# Revit family: Солід_Eng
name_source: partatom
category: Mechanical Equipment
units: mm (PartAtom-declared; Revit-internal decimal feet)

## family parameters
Always vertical = Yes
Classification = None
Cut with Voids When Loaded = No
Part Type = Normal
Room Calculation Point = No
Round Connector Dimension = Use Diameter
Shared = No
Work Plane-Based = No

## types (4) — shared parameters
00_20_Manufacturer = Vents
00_20_Name = Axial fan
Amperage = 0 A
Casing Material = Plastic, opaque, white
L1 = 38 mm  [stored 0.124672 ft]
Load Classification = HVAC
Maintenance zone material = <By Category>
Manufacturer = Vents
Number of Fase = 1
URL = https://ventilation-system.com
Voltage = 230 V
zero-valued in all types: Default Elevation

## per-type parameters (varying)
| type | B | D | Diameter | Dy | Frequency | H | Height | L | L2 | Length | Maximum Air Flow | Power | Sound pressure level at 3 m distance | Weight | Width |
| 100 Solid | 160 mm  [stored 0.524934 ft] | 100 mm  [stored 0.328084 ft] | 100 mm  [stored 0.328084 ft] | 95 mm  [stored 0.31168 ft] | 50 Hz | 160 mm  [stored 0.524934 ft] | 160 mm  [stored 0.524934 ft] | 79 mm | 41 mm  [stored 0.134514 ft] | 79 mm | 85.0 m³/h | 8 W | 27 дБА | 0.51 kg | 160 mm  [stored 0.524934 ft] |
| 125 Solid | 180 mm  [stored 0.590551 ft] | 125 mm  [stored 0.410105 ft] | 125 mm  [stored 0.410105 ft] | 120 mm  [stored 0.393701 ft] | 50 Hz | 180 mm  [stored 0.590551 ft] | 180 mm  [stored 0.590551 ft] | 85 mm  [stored 0.278871 ft] | 47 mm  [stored 0.154199 ft] | 85 mm  [stored 0.278871 ft] | 155.0 m³/h | 18 W | 32 дБА | 0.75 kg | 180 mm  [stored 0.590551 ft] |
| 100 Solid (220 В/60 Hz) | 160 mm  [stored 0.524934 ft] | 100 mm  [stored 0.328084 ft] | 100 mm  [stored 0.328084 ft] | 95 mm  [stored 0.31168 ft] | 60 Hz | 160 mm  [stored 0.524934 ft] | 160 mm  [stored 0.524934 ft] | 79 mm | 41 mm  [stored 0.134514 ft] | 79 mm | 85.0 m³/h | 8 W | 27 дБА | 0.51 kg | 160 mm  [stored 0.524934 ft] |
| 125 Solid (220 В/60 Hz) | 180 mm  [stored 0.590551 ft] | 125 mm  [stored 0.410105 ft] | 125 mm  [stored 0.410105 ft] | 120 mm  [stored 0.393701 ft] | 60 Hz | 180 mm  [stored 0.590551 ft] | 180 mm  [stored 0.590551 ft] | 85 mm  [stored 0.278871 ft] | 47 mm  [stored 0.154199 ft] | 85 mm  [stored 0.278871 ft] | 155.0 m³/h | 18 W | 32 дБА | 0.75 kg | 180 mm  [stored 0.590551 ft] |

note: column(s) folded — value = type name in every type: 00_20_Type

note: [stored X ft] marks values corroborated as IEEE doubles in the binary element streams (Revit-internal decimal feet)
